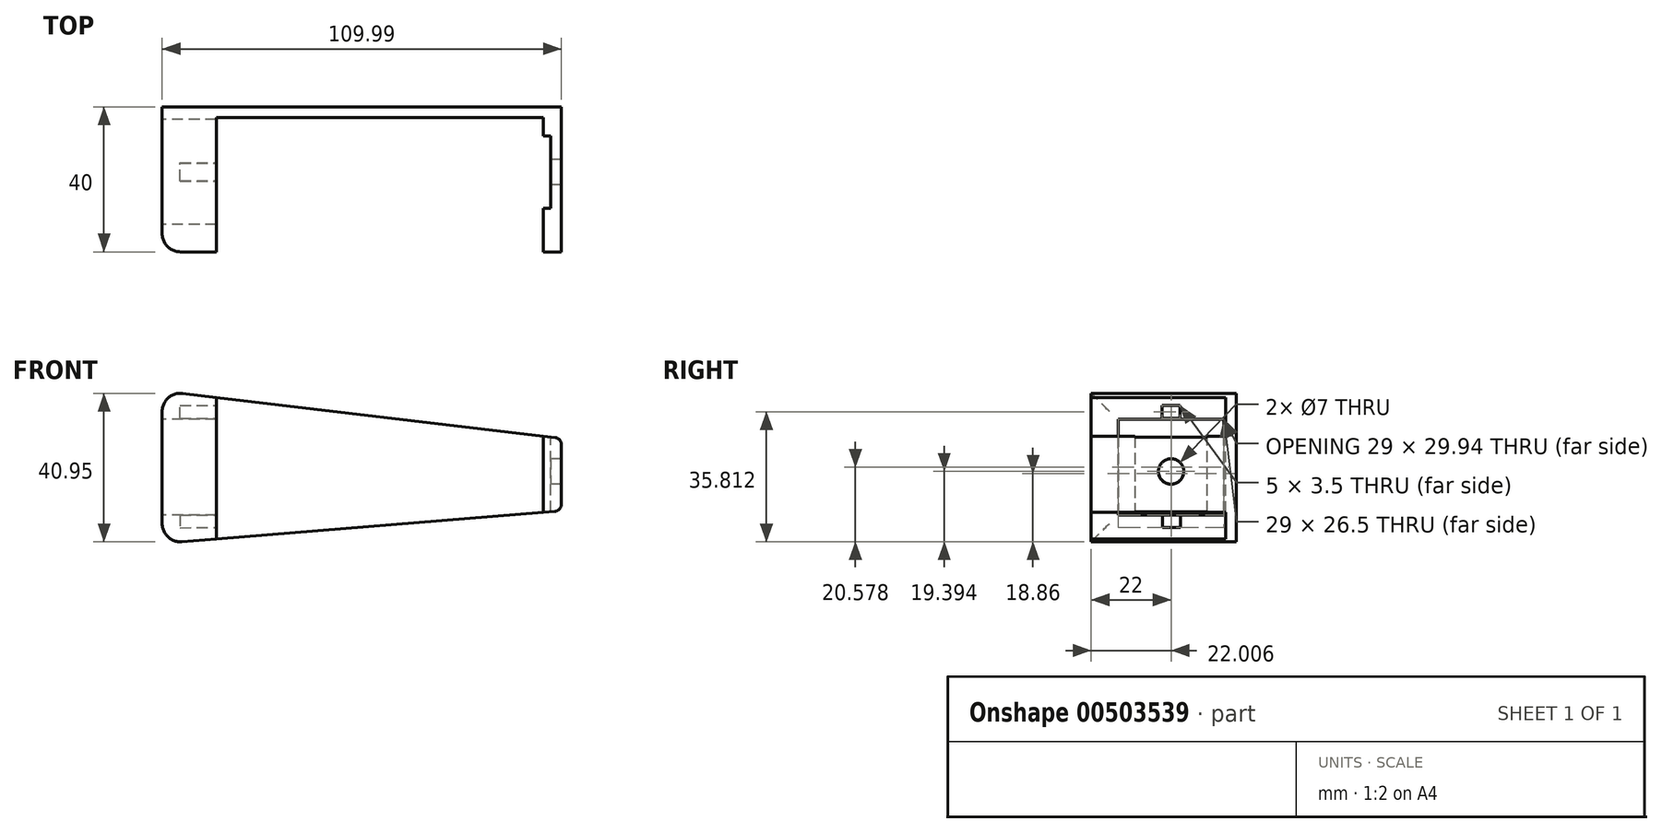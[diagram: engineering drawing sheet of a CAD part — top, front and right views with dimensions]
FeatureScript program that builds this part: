
annotation { "Feature Type Name" : "Feature", "Feature Type Description" : "" }
export const myFeature = defineFeature(function(context is Context, id is Id, definition is map)
    precondition{}
    {
        {
            var Q0;
            Q0=qCreatedBy(makeId("Front.planeOp"),FACE);
            var sketch = newSketch(context, id + "F0", { "sketchPlane" : qUnion([Q0])});
            skLineSegment(sketch, "E0", {"start": v(-50, 0) * mm, "end": v(-50, 42) * mm});
            skLineSegment(sketch, "E1", {"start": v(59.96, 18.95) * mm, "end": v(60, 28.95) * mm});
            skLineSegment(sketch, "E2", {"start": v(59.96, 18.95) * mm, "end": v(59.96, 8.95) * mm});
            skLineSegment(sketch, "E3", {"start": v(59.96, 8.95) * mm, "end": v(-50, 0) * mm});
            skLineSegment(sketch, "E4", {"start": v(-50, 42) * mm, "end": v(60, 28.95) * mm});
            skLineSegment(sketch, "E5", {"start": v(-50, 0) * mm, "end": v(-35.05, 1.21) * mm});
            skLineSegment(sketch, "E6", {"start": v(-50, 42) * mm, "end": v(-35.1, 40.23) * mm});
            skLineSegment(sketch, "E7", {"start": v(-35.1, 40.23) * mm, "end": v(-35.05, 1.21) * mm});
            skLineSegment(sketch, "E8", {"start": v(59.96, 8.95) * mm, "end": v(54.98, 8.54) * mm});
            skLineSegment(sketch, "E9", {"start": v(60, 28.95) * mm, "end": v(55.04, 29.53) * mm});
            skLineSegment(sketch, "E10", {"start": v(55.04, 29.53) * mm, "end": v(54.98, 8.54) * mm});
            skSolve(sketch);
        }
        {
            var Q0;
            Q0=makeQuery(id+"F0.imprint","IMPRINT",FACE,{"disambiguationData":[TD([[makeQuery(id+"F0.imprint","IMPRINT",EDGE,{"derivedFrom":sQuery(id+"F0.wireOp",EDGE,"E3")}),-1.0]])]});
            var Q1;
            Q1=makeQuery(id+"F0.imprint","IMPRINT",FACE,{"disambiguationData":[TD([[makeQuery(id+"F0.imprint","IMPRINT",EDGE,{"derivedFrom":sQuery(id+"F0.wireOp",EDGE,"E0")}),-1.0]])]});
            var Q2;
            Q2=makeQuery(id+"F0.imprint","IMPRINT",FACE,{"disambiguationData":[TD([[makeQuery(id+"F0.imprint","IMPRINT",EDGE,{"derivedFrom":sQuery(id+"F0.wireOp",EDGE,"E1")}),1.0]])]});
            extrude(context, id + "F1", {"entities" : qUnion([Q0, Q1, Q2]), "depth" : 40 * mm});
        }
        {
            var Q0;
            Q0=makeQuery(id+"F1.opExtrude","CAP_FACE",FACE,{"disambiguationData":[OSD([sQuery(id+"F0.wireOp",EDGE,"E0"),sQuery(id+"F0.wireOp",EDGE,"E1"),sQuery(id+"F0.wireOp",EDGE,"E2"),sQuery(id+"F0.wireOp",EDGE,"E3"),sQuery(id+"F0.wireOp",EDGE,"E4"),sQuery(id+"F0.wireOp",EDGE,"E5"),sQuery(id+"F0.wireOp",EDGE,"E6"),sQuery(id+"F0.wireOp",EDGE,"E8"),sQuery(id+"F0.wireOp",EDGE,"E9")])],"isStart":false});
            var sketch = newSketch(context, id + "F2", { "sketchPlane" : qUnion([Q0])});
            skLineSegment(sketch, "E11", {"start": v(-50, 0) * mm, "end": v(-35.05, 1.21) * mm});
            skLineSegment(sketch, "E12", {"start": v(-50, 42) * mm, "end": v(-35.1, 40.23) * mm});
            skLineSegment(sketch, "E13", {"start": v(60, 28.95) * mm, "end": v(55.04, 29.53) * mm});
            skLineSegment(sketch, "E14", {"start": v(-35.05, 1.21) * mm, "end": v(-35.1, 40.23) * mm});
            skLineSegment(sketch, "E15", {"start": v(59.96, 8.95) * mm, "end": v(54.98, 8.54) * mm});
            skLineSegment(sketch, "E16", {"start": v(54.98, 8.54) * mm, "end": v(55.04, 29.53) * mm});
            skSolve(sketch);
        }
        {
            var Q0;
            {var subQ0=sQuery(id+"F2.wireOp",EDGE,"E14");Q0=makeQuery(id+"F2.imprint","IMPRINT",FACE,{"disambiguationData":[TD([[makeQuery(id+"F2.imprint","IMPRINT",EDGE,{"derivedFrom":subQ0}),-1.0]])]});}
            extrude(context, id + "F3", {"entities" : qUnion([Q0]), "operationType" : NewBodyOperationType.REMOVE, "oppositeDirection" : true, "depth" : 37 * mm});
        }
        {
            var Q0;
            Q0=makeQuery(id+"F1.opExtrude","SWEPT_FACE",FACE,{"disambiguationData":[OSD([sQuery(id+"F0.wireOp",EDGE,"E0")])]});
            var sketch = newSketch(context, id + "F4", { "sketchPlane" : qUnion([Q0])});
            skLineSegment(sketch, "E17", {"start": v(0, 42) * mm, "end": v(0, 21) * mm});
            skLineSegment(sketch, "E18", {"start": v(3.5, 21) * mm, "end": v(3.5, 7.75) * mm});
            skLineSegment(sketch, "E19", {"start": v(3.5, 7.75) * mm, "end": v(32.5, 7.75) * mm});
            skLineSegment(sketch, "E20", {"start": v(32.5, 7.75) * mm, "end": v(32.5, 34.25) * mm});
            skLineSegment(sketch, "E21", {"start": v(32.5, 34.25) * mm, "end": v(3.5, 34.25) * mm});
            skLineSegment(sketch, "E22", {"start": v(3.5, 34.25) * mm, "end": v(3.5, 21) * mm});
            skSolve(sketch);
        }
        {
            var Q0;
            Q0=makeQuery(id+"F4.imprint","IMPRINT",FACE,{"disambiguationData":[TD([[makeQuery(id+"F4.imprint","IMPRINT",EDGE,{"derivedFrom":sQuery(id+"F4.wireOp",EDGE,"E18")}),1.0]])]});
            extrude(context, id + "F5", {"entities" : qUnion([Q0]), "operationType" : NewBodyOperationType.REMOVE, "oppositeDirection" : true, "depth" : 25 * mm});
        }
        {
            var Q0;
            Q0=makeQuery(id+"F1.opExtrude","SWEPT_EDGE",EDGE,{"disambiguationData":[OSD([sQuery(id+"F0.wireOp",EDGE,"E0"),sQuery(id+"F0.wireOp",EDGE,"E6")])]});
            var Q1;
            Q1=makeQuery(id+"F1.opExtrude","SWEPT_EDGE",EDGE,{"disambiguationData":[OSD([sQuery(id+"F0.wireOp",EDGE,"E0"),sQuery(id+"F0.wireOp",EDGE,"E5")])]});
            var Q2;
            Q2=makeQuery(id+"F1.opExtrude","CAP_EDGE",EDGE,{"disambiguationData":[OSD([sQuery(id+"F0.wireOp",EDGE,"E0")])],"isStart":false});
            fillet(context, id + "F6", {"entities" : qUnion([Q0, Q1, Q2]), "radius" : 5 * mm, "tangentPropagation" : true, "allowEdgeOverflow" : false});
        }
        {
            var Q0;
            Q0=makeQuery(id+"F1.opExtrude","SWEPT_EDGE",EDGE,{"disambiguationData":[OSD([sQuery(id+"F0.wireOp",EDGE,"E1"),sQuery(id+"F0.wireOp",EDGE,"E9")])]});
            var Q1;
            Q1=makeQuery(id+"FO1bqp8k0jweBNm_1.boolean.opBoolean","COPY",EDGE,{"derivedFrom":makeQuery(id+"FO1bqp8k0jweBNm_1.opExtrude","CAP_EDGE",EDGE,{"disambiguationData":[OSD([sQuery(id+"F0.wireOp",EDGE,"E1")])],"isStart":false})});
            var Q2;
            Q2=makeQuery(id+"F1.opExtrude","SWEPT_EDGE",EDGE,{"disambiguationData":[OSD([sQuery(id+"F0.wireOp",EDGE,"E2"),sQuery(id+"F0.wireOp",EDGE,"E8")])]});
            var Q3;
            Q3=makeQuery(id+"FO1bqp8k0jweBNm_1.boolean.opBoolean","COPY",EDGE,{"derivedFrom":makeQuery(id+"FO1bqp8k0jweBNm_1.opExtrude","CAP_EDGE",EDGE,{"disambiguationData":[OSD([sQuery(id+"F0.wireOp",EDGE,"E2")])],"isStart":false})});
            fillet(context, id + "F7", {"entities" : qUnion([Q0, Q1, Q2, Q3]), "radius" : 2 * mm, "tangentPropagation" : true, "allowEdgeOverflow" : false});
        }
        {
            var Q0;
            Q0=makeQuery(id+"F3.boolean.opBoolean","COPY",FACE,{"derivedFrom":makeQuery(id+"F3.opExtrude","SWEPT_FACE",FACE,{"disambiguationData":[OSD([sQuery(id+"F2.wireOp",EDGE,"E14")])]})});
            var sketch = newSketch(context, id + "F8", { "sketchPlane" : qUnion([Q0])});
            skLineSegment(sketch, "E23", {"start": v(-32.5, 34.3) * mm, "end": v(-20.5, 34.3) * mm});
            skSolve(sketch);
        }
        {
            var Q0;
            {var subQ1=sQuery(id+"F8.wireOp",EDGE,"E23");Q0=makeQuery(id+"F8.imprint","IMPRINT",FACE,{"disambiguationData":[TD([[makeQuery(id+"F8.imprint","IMPRINT",EDGE,{"derivedFrom":subQ1}),-1.0]])]});}
            var sketch = newSketch(context, id + "F9", { "sketchPlane" : qUnion([Q0])});
            skLineSegment(sketch, "E24", {"start": v(-20.5, 34.53) * mm, "end": v(-20.5, 38.03) * mm});
            skLineSegment(sketch, "E25", {"start": v(-20.5, 38.03) * mm, "end": v(-15.5, 38.03) * mm});
            skLineSegment(sketch, "E26", {"start": v(-20.5, 34.53) * mm, "end": v(-15.5, 34.53) * mm});
            skLineSegment(sketch, "E27", {"start": v(-15.5, 34.53) * mm, "end": v(-15.5, 38.03) * mm});
            skLineSegment(sketch, "E28", {"start": v(-20.38, 7.86) * mm, "end": v(-20.38, 4.36) * mm});
            skLineSegment(sketch, "E29", {"start": v(-20.38, 4.36) * mm, "end": v(-15.38, 4.36) * mm});
            skLineSegment(sketch, "E30", {"start": v(-15.38, 7.86) * mm, "end": v(-20.38, 7.86) * mm});
            skLineSegment(sketch, "E31", {"start": v(-15.38, 7.86) * mm, "end": v(-15.38, 4.36) * mm});
            skSolve(sketch);
        }
        {
            var Q0;
            Q0=makeQuery(id+"F9.imprint","IMPRINT",FACE,{"disambiguationData":[TD([[makeQuery(id+"F9.imprint","IMPRINT",EDGE,{"derivedFrom":sQuery(id+"F9.wireOp",EDGE,"E24")}),-1.0]])]});
            var Q1;
            {var subQ0=sQuery(id+"F9.wireOp",EDGE,"E29");Q1=makeQuery(id+"F9.imprint","IMPRINT",FACE,{"disambiguationData":[TD([[makeQuery(id+"F9.imprint","IMPRINT",EDGE,{"derivedFrom":subQ0}),1.0]])]});}
            extrude(context, id + "F10", {"entities" : qUnion([Q0, Q1]), "operationType" : NewBodyOperationType.REMOVE, "oppositeDirection" : true, "depth" : 10 * mm, "offsetDistance" : 25 * mm});
        }
        {
            var Q0;
            Q0=makeQuery(id+"F3.boolean.opBoolean","COPY",FACE,{"derivedFrom":makeQuery(id+"F3.opExtrude","SWEPT_FACE",FACE,{"disambiguationData":[OSD([sQuery(id+"F2.wireOp",EDGE,"E16")])]})});
            var sketch = newSketch(context, id + "F11", { "sketchPlane" : qUnion([Q0])});
            skLineSegment(sketch, "E32", {"start": v(3, 8.7) * mm, "end": v(8, 8.7) * mm});
            skLineSegment(sketch, "E33", {"start": v(8, 8.7) * mm, "end": v(8, 29.7) * mm});
            skLineSegment(sketch, "E34", {"start": v(8, 29.7) * mm, "end": v(28, 29.7) * mm});
            skLineSegment(sketch, "E35", {"start": v(28, 29.7) * mm, "end": v(28, 8.7) * mm});
            skLineSegment(sketch, "E36", {"start": v(28, 8.7) * mm, "end": v(8, 8.7) * mm});
            skSolve(sketch);
        }
        {
            var Q0;
            Q0=makeQuery(id+"F11.imprint","IMPRINT",FACE,{"disambiguationData":[TD([[makeQuery(id+"F11.imprint","IMPRINT",EDGE,{"derivedFrom":sQuery(id+"F11.wireOp",EDGE,"E33")}),-1.0]])]});
            extrude(context, id + "F12", {"entities" : qUnion([Q0]), "operationType" : NewBodyOperationType.REMOVE, "oppositeDirection" : true, "depth" : 2 * mm, "offsetDistance" : 25 * mm});
        }
        {
            var Q0;
            Q0=makeQuery(id+"F12.boolean.opBoolean","COPY",FACE,{"derivedFrom":makeQuery(id+"F12.opExtrude","CAP_FACE",FACE,{"disambiguationData":[OSD([sQuery(id+"F11.wireOp",EDGE,"E33"),sQuery(id+"F11.wireOp",EDGE,"E34"),sQuery(id+"F11.wireOp",EDGE,"E35"),sQuery(id+"F11.wireOp",EDGE,"E36")])],"isStart":false})});
            var sketch = newSketch(context, id + "F13", { "sketchPlane" : qUnion([Q0])});
            skCircle(sketch, "E37", {"center": v(18, 19.98) * mm, "radius": 3.5 * mm});
            skPoint(sketch, "E37.centerSnap0", {"position": v(18, 29.46) * mm});
            skSolve(sketch);
        }
        {
            var Q0;
            Q0=makeQuery(id+"F13.imprint","IMPRINT",FACE,{"disambiguationData":[TD([[makeQuery(id+"F13.imprint","IMPRINT",EDGE,{"derivedFrom":sQuery(id+"F13.wireOp",EDGE,"E37")}),1.0]])]});
            extrude(context, id + "F14", {"entities" : qUnion([Q0]), "operationType" : NewBodyOperationType.REMOVE, "oppositeDirection" : true, "depth" : 25 * mm, "offsetDistance" : 25 * mm});
        }
    });
